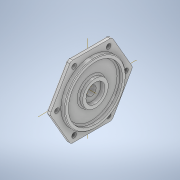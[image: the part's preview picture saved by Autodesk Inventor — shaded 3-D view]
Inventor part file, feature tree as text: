
AUTODESK INVENTOR PART (.ipt)
format: ipt  version: 2021.1 (Build 251245000, 245)  size: 235,008 bytes
history: native  units: in
note: dims shown in document units (in); Inventor stores cm internally (conversion verified against a paired STEP export)
features: extrude x5, sketch x4, fillet x3, chamfer x1
ambient origin geometry x8: Origin, YZ Plane, XZ Plane, XY Plane, X Axis, Y Axis, Z Axis, Center Point
bodies: Solid1 (feature_tree)
feature tree (13):
  extrude  "Extrusion1"  Depth=0.5in
  extrude  "Extrusion2"  Depth=1.4in
  extrude  "Extrusion3"  Depth=0.4in
  fillet  "Fillet1"  Radius=4.6in
  fillet  "Fillet2"  Radius=0.4in
  sketch  "Sketch4"  dims[d12=0.4in d13=0.2in d14=10.2in d15=2.8in d16=3.8in d17=8.0in d18=9.0in d19=0.7in d20=2.3622in d22=360.0deg d24=0.6in d25=0.0in d26=0.0in d27=0.0in d28=0.2in d29=0.1in d30=0.125in d31=45.0deg]
  extrude  "Extrusion4"  Depth=0.2in
  extrude  "Extrusion5"  Depth=0.2in
  fillet  "Fillet3"  Radius=2.8in
  chamfer  "Chamfer1"  Distance=3.8in
  sketch  "Sketch1"  dims[d0=10.6in d1=0.5in]
  sketch  "Sketch2"  dims[d2=0.6in d3=0.0in d5=1.4in]
  sketch  "Sketch3"  dims[d6=0.0in d7=0.0in d8=4.6in d9=4.6in d10=0.4in d11=0.0in]
